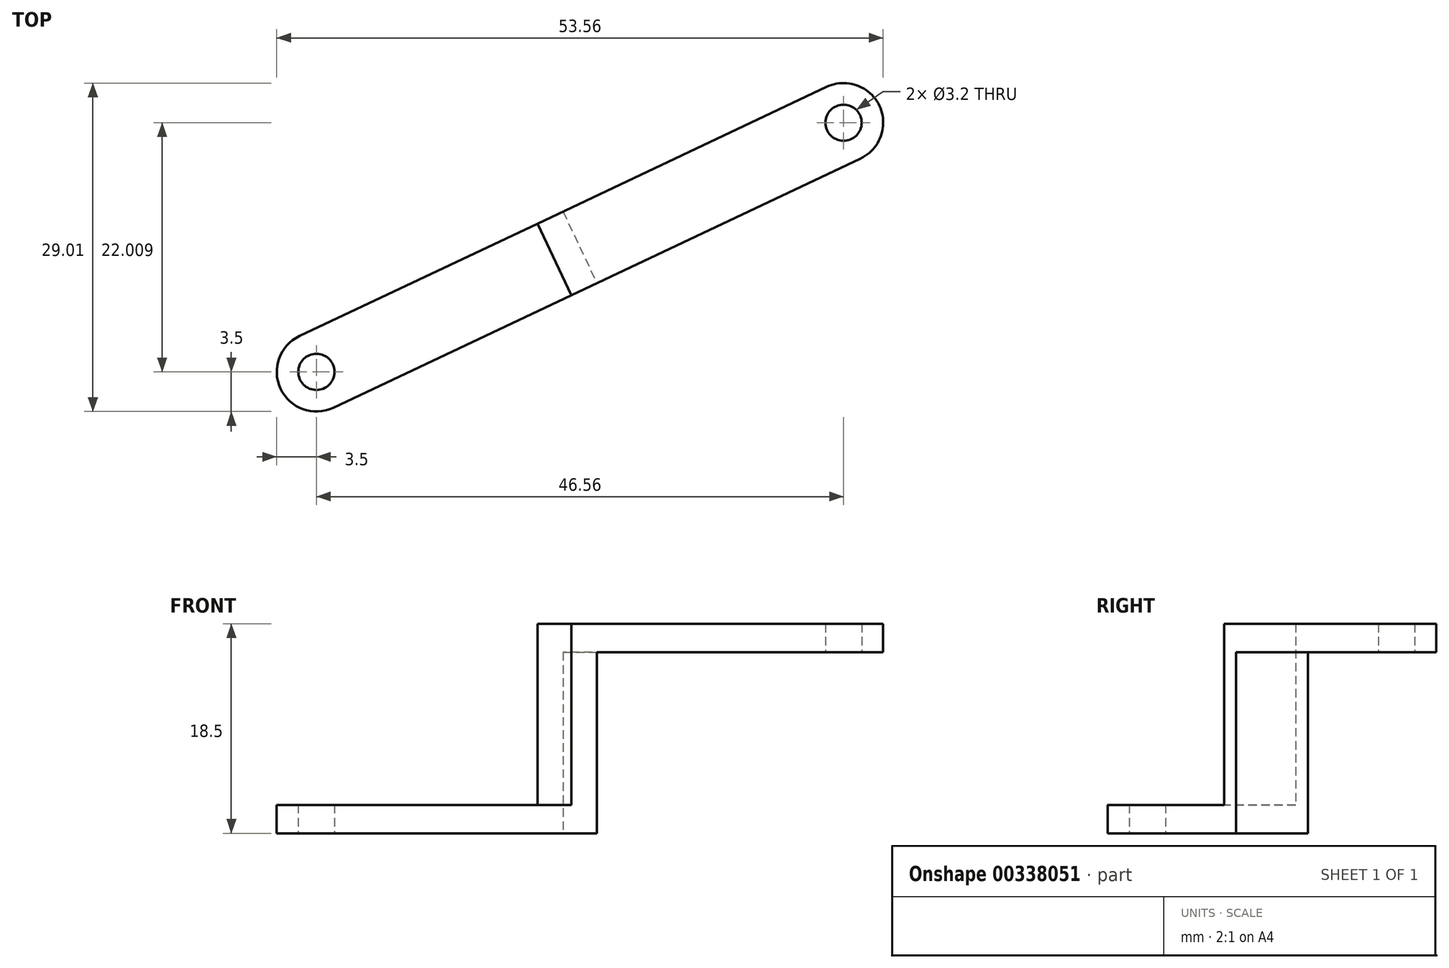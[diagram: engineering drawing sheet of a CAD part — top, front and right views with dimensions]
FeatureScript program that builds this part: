
annotation { "Feature Type Name" : "Feature", "Feature Type Description" : "" }
export const myFeature = defineFeature(function(context is Context, id is Id, definition is map)
    precondition{}
    {
        {
            var Q0;
            Q0=qCreatedBy(makeId("Top.planeOp"),FACE);
            cPlane(context, id + "F0", {"entities" : qUnion([Q0]), "cplaneType" : CPlaneType.OFFSET, "offset" : 16 * mm, "width" : 150 * mm, "height" : 150 * mm});
        }
        {
            var Q0;
            Q0=qCreatedBy(id+"F0.planeOp",FACE);
            var sketch = newSketch(context, id + "F1", { "sketchPlane" : qUnion([Q0])});
            skLineSegment(sketch, "E0", {"start": v(0, 0) * mm, "end": v(46.56, 22) * mm, "construction": true});
            skCircle(sketch, "E1", {"center": v(46.56, 22) * mm, "radius": 1.6 * mm});
            skCircle(sketch, "E2", {"center": v(46.56, 22) * mm, "radius": 3.5 * mm});
            skLineSegment(sketch, "E3", {"start": v(45.06, 25.17) * mm, "end": v(21.78, 14.17) * mm});
            skLineSegment(sketch, "E4.MirrorCS", {"start": v(48.06, 18.84) * mm, "end": v(24.78, 7.84) * mm});
            skLineSegment(sketch, "E5", {"start": v(21.78, 14.17) * mm, "end": v(24.78, 7.84) * mm});
            skSolve(sketch);
        }
        {
            var Q0;
            Q0 = qSketchRegion(id + "F1", true);
            extrude(context, id + "F2", {"entities" : qUnion([Q0]), "depth" : 2.5 * mm});
        }
        {
            var Q0;
            Q0=makeQuery(id+"F2.opExtrude","SWEPT_FACE",FACE,{"disambiguationData":[OSD([sQuery(id+"F1.wireOp",EDGE,"E5")])]});
            var sketch = newSketch(context, id + "F3", { "sketchPlane" : qUnion([Q0])});
            skLineSegment(sketch, "E6.bottom", {"start": v(-3.5, 18.5) * mm, "end": v(3.5, 18.5) * mm});
            skLineSegment(sketch, "E6.top", {"start": v(-3.5, 0) * mm, "end": v(3.5, 0) * mm});
            skLineSegment(sketch, "E6.left", {"start": v(-3.5, 18.5) * mm, "end": v(-3.5, 0) * mm});
            skLineSegment(sketch, "E6.right", {"start": v(3.5, 18.5) * mm, "end": v(3.5, 0) * mm});
            skSolve(sketch);
        }
        {
            var Q0;
            Q0 = qSketchRegion(id + "F3", true);
            extrude(context, id + "F4", {"entities" : qUnion([Q0]), "operationType" : NewBodyOperationType.ADD, "depth" : 2.5 * mm});
        }
        {
            var Q0;
            Q0=qCreatedBy(makeId("Top.planeOp"),FACE);
            var sketch = newSketch(context, id + "F5", { "sketchPlane" : qUnion([Q0])});
            skCircle(sketch, "E7", {"center": v(0, 0) * mm, "radius": 1.6 * mm});
            skCircle(sketch, "E8", {"center": v(0, 0) * mm, "radius": 3.5 * mm});
            skLineSegment(sketch, "E9", {"start": v(0, 0) * mm, "end": v(22.82, 10.79) * mm, "construction": true});
            skLineSegment(sketch, "E10", {"start": v(-1.5, 3.16) * mm, "end": v(19.52, 13.1) * mm});
            skLineSegment(sketch, "E11.MirrorCS", {"start": v(1.5, -3.16) * mm, "end": v(22.52, 6.77) * mm});
            skLineSegment(sketch, "E12.0", {"start": v(19.52, 13.1) * mm, "end": v(22.52, 6.77) * mm});
            skSolve(sketch);
        }
        {
            var Q0;
            Q0 = qSketchRegion(id + "F5", true);
            extrude(context, id + "F6", {"entities" : qUnion([Q0]), "operationType" : NewBodyOperationType.ADD, "depth" : 2.5 * mm});
        }
    });
